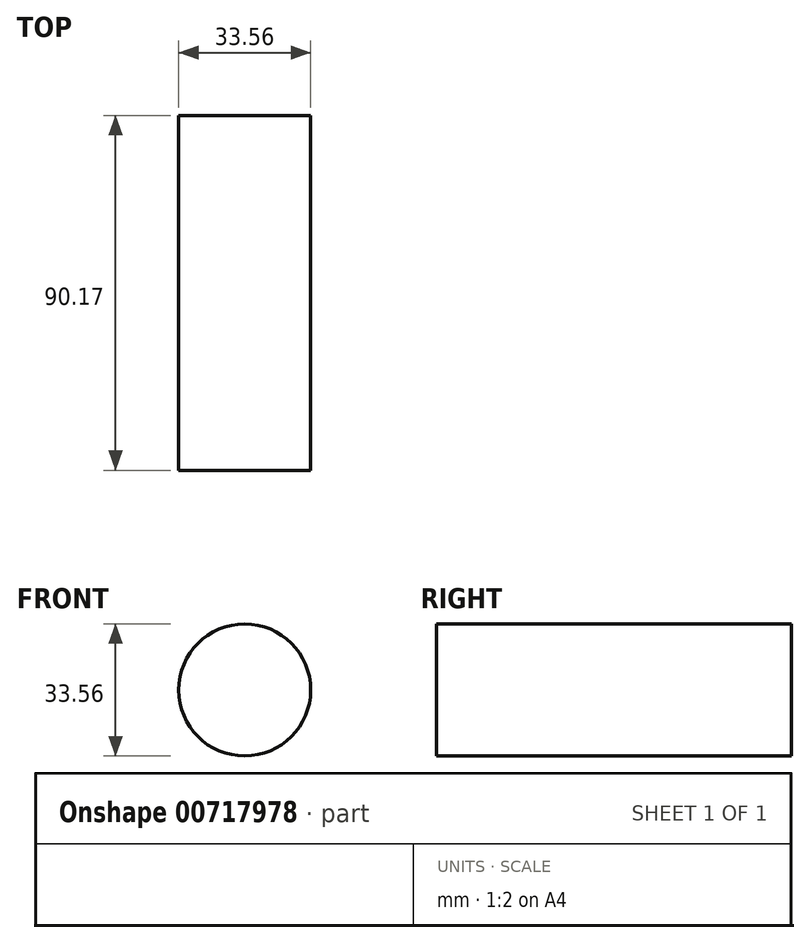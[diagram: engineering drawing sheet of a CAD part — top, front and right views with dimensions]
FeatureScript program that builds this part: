
annotation { "Feature Type Name" : "Feature", "Feature Type Description" : "" }
export const myFeature = defineFeature(function(context is Context, id is Id, definition is map)
    precondition{}
    {
        {
            var Q0;
            Q0=qCreatedBy(makeId("Front.planeOp"),FACE);
            var sketch = newSketch(context, id + "F0", { "sketchPlane" : qUnion([Q0])});
            skCircle(sketch, "E0", {"center": v(-54.77, 56.58) * mm, "radius": 16.78 * mm});
            skSolve(sketch);
        }
        {
            var Q0;
            Q0 = qSketchRegion(id + "F0", true);
            extrude(context, id + "F1", {"entities" : qUnion([Q0]), "depth" : 90.17 * mm, "offsetDistance" : 25.4 * mm});
        }
    });
